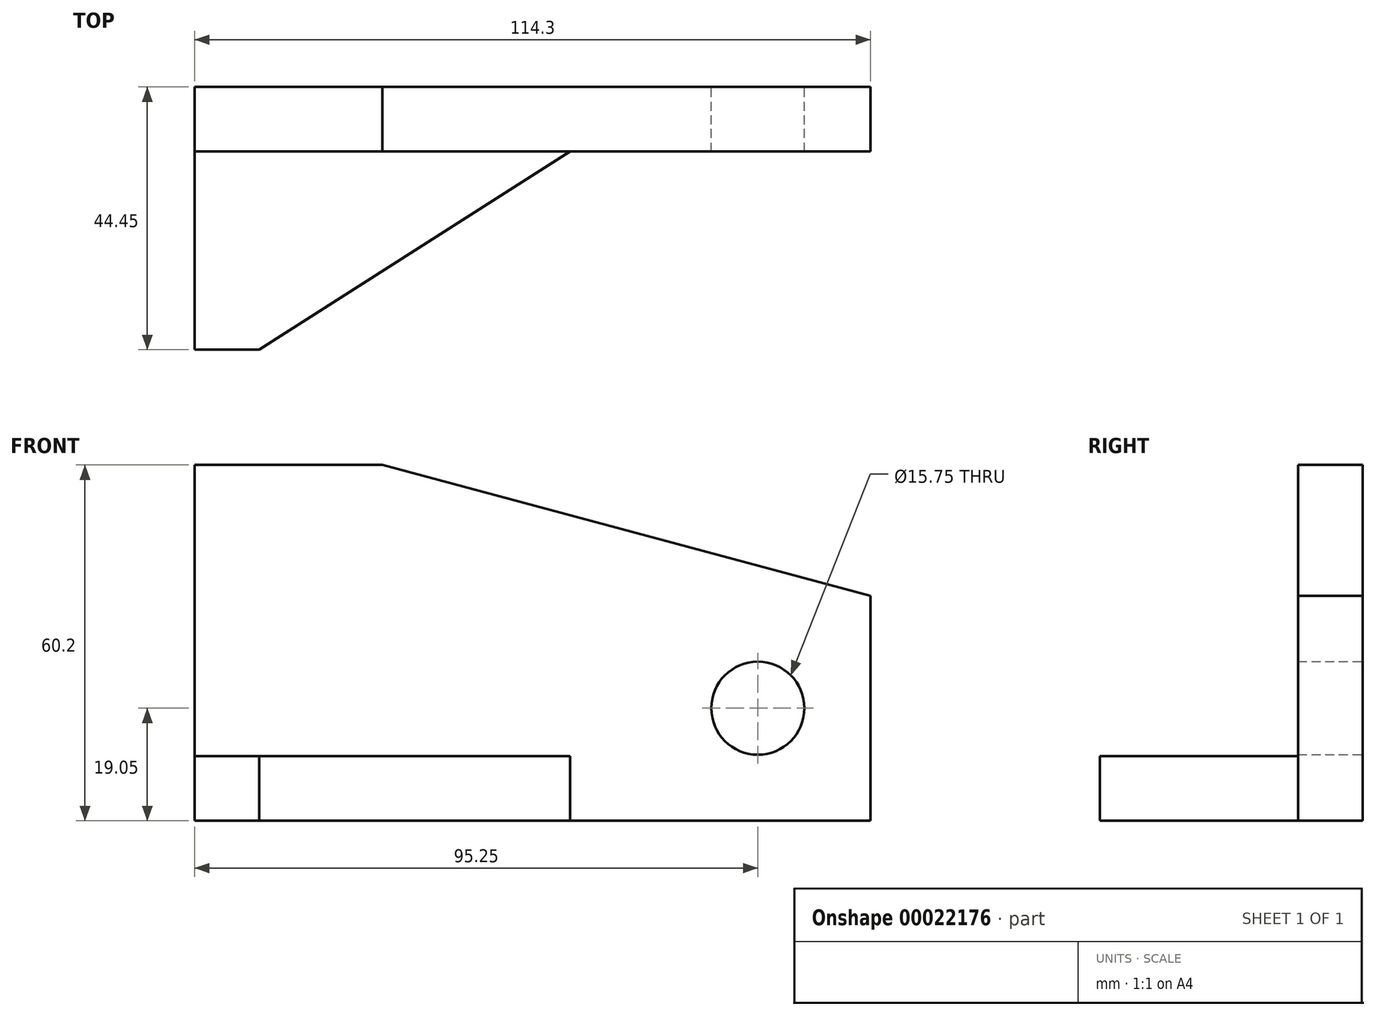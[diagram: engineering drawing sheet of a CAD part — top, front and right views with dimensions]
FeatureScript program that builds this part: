
annotation { "Feature Type Name" : "Feature", "Feature Type Description" : "" }
export const myFeature = defineFeature(function(context is Context, id is Id, definition is map)
    precondition{}
    {
        {
            var Q0;
            Q0=qCreatedBy(makeId("Front.planeOp"),FACE);
            var sketch = newSketch(context, id + "F0", { "sketchPlane" : qUnion([Q0])});
            skLineSegment(sketch, "E0.bottom", {"start": v(0, 60.2) * mm, "end": v(114.3, 60.2) * mm});
            skLineSegment(sketch, "E0.top", {"start": v(0, 0) * mm, "end": v(114.3, 0) * mm});
            skLineSegment(sketch, "E0.left", {"start": v(0, 60.2) * mm, "end": v(0, 0) * mm});
            skLineSegment(sketch, "E0.right", {"start": v(114.3, 60.2) * mm, "end": v(114.3, 0) * mm});
            skLineSegment(sketch, "E1", {"start": v(31.75, 60.2) * mm, "end": v(114.3, 38.08) * mm});
            skCircle(sketch, "E2", {"center": v(95.25, 19.05) * mm, "radius": 7.87 * mm});
            skLineSegment(sketch, "E3", {"start": v(114.3, 0) * mm, "end": v(63.5, 0) * mm});
            skSolve(sketch);
        }
        {
            var Q0;
            Q0=qCreatedBy(makeId("Right.planeOp"),FACE);
            var sketch = newSketch(context, id + "F1", { "sketchPlane" : qUnion([Q0])});
            skLineSegment(sketch, "E4.bottom", {"start": v(0, 0) * mm, "end": v(-44.45, 0) * mm});
            skLineSegment(sketch, "E4.top", {"start": v(0, 50.8) * mm, "end": v(-44.45, 50.8) * mm});
            skLineSegment(sketch, "E4.left", {"start": v(0, 0) * mm, "end": v(0, 50.8) * mm});
            skLineSegment(sketch, "E4.right", {"start": v(-44.45, 0) * mm, "end": v(-44.45, 50.8) * mm});
            skLineSegment(sketch, "E5", {"start": v(-27.88, 50.8) * mm, "end": v(-44.45, 22.1) * mm});
            skLineSegment(sketch, "E6.bottom", {"start": v(-44.45, 0) * mm, "end": v(0, 0) * mm});
            skLineSegment(sketch, "E6.top", {"start": v(-44.45, 10.92) * mm, "end": v(0, 10.92) * mm});
            skLineSegment(sketch, "E6.left", {"start": v(-44.45, 0) * mm, "end": v(-44.45, 10.92) * mm});
            skLineSegment(sketch, "E6.right", {"start": v(0, 0) * mm, "end": v(0, 10.92) * mm});
            skSolve(sketch);
        }
        {
            var Q0;
            Q0=qCreatedBy(makeId("Top.planeOp"),FACE);
            var sketch = newSketch(context, id + "F2", { "sketchPlane" : qUnion([Q0])});
            skLineSegment(sketch, "E7.bottom", {"start": v(0, 0) * mm, "end": v(63.5, 0) * mm});
            skLineSegment(sketch, "E7.top", {"start": v(0, -44.45) * mm, "end": v(63.5, -44.45) * mm});
            skLineSegment(sketch, "E7.left", {"start": v(0, 0) * mm, "end": v(0, -44.45) * mm});
            skLineSegment(sketch, "E7.right", {"start": v(63.5, 0) * mm, "end": v(63.5, -44.45) * mm});
            skLineSegment(sketch, "E8", {"start": v(0, -44.45) * mm, "end": v(10.92, -44.45) * mm});
            skLineSegment(sketch, "E9", {"start": v(63.5, 0) * mm, "end": v(63.5, -10.92) * mm});
            skLineSegment(sketch, "E10", {"start": v(10.92, -44.45) * mm, "end": v(63.5, -10.92) * mm});
            skSolve(sketch);
        }
        {
            var Q0;
            Q0=makeQuery(id+"F0.imprint","IMPRINT",FACE,{"disambiguationData":[TD([[makeQuery(id+"F0.imprint","IMPRINT",EDGE,{"derivedFrom":sQuery(id+"F0.wireOp",EDGE,"E0.top")}),1.0]])]});
            extrude(context, id + "F3", {"entities" : qUnion([Q0]), "depth" : 10.92 * mm});
        }
        {
            var Q0;
            Q0=makeQuery(id+"F1.imprint","IMPRINT",FACE,{"disambiguationData":[TD([[makeQuery(id+"F1.imprint","IMPRINT",EDGE,{"derivedFrom":sQuery(id+"F1.wireOp",EDGE,"E6.bottom")}),1.0]])]});
            var Q1;
            {var subQ3=sQuery(id+"F1.wireOp",EDGE,"E4.left");Q1=makeQuery(id+"F1.imprint","IMPRINT",FACE,{"disambiguationData":[TD([[makeQuery(id+"F1.imprint","IMPRINT",EDGE,{"derivedFrom":subQ3}),1.0]])]});}
            extrude(context, id + "F4", {"entities" : qUnion([Q0, Q1]), "operationType" : NewBodyOperationType.ADD, "depth" : 10.92 * mm});
        }
        {
            var Q0;
            Q0=makeQuery(id+"F2.imprint","IMPRINT",FACE,{"disambiguationData":[TD([[makeQuery(id+"F2.imprint","IMPRINT",EDGE,{"derivedFrom":sQuery(id+"F2.wireOp",EDGE,"E7.bottom")}),-1.0]])]});
            extrude(context, id + "F5", {"entities" : qUnion([Q0]), "operationType" : NewBodyOperationType.ADD, "depth" : 10.92 * mm});
        }
    });
